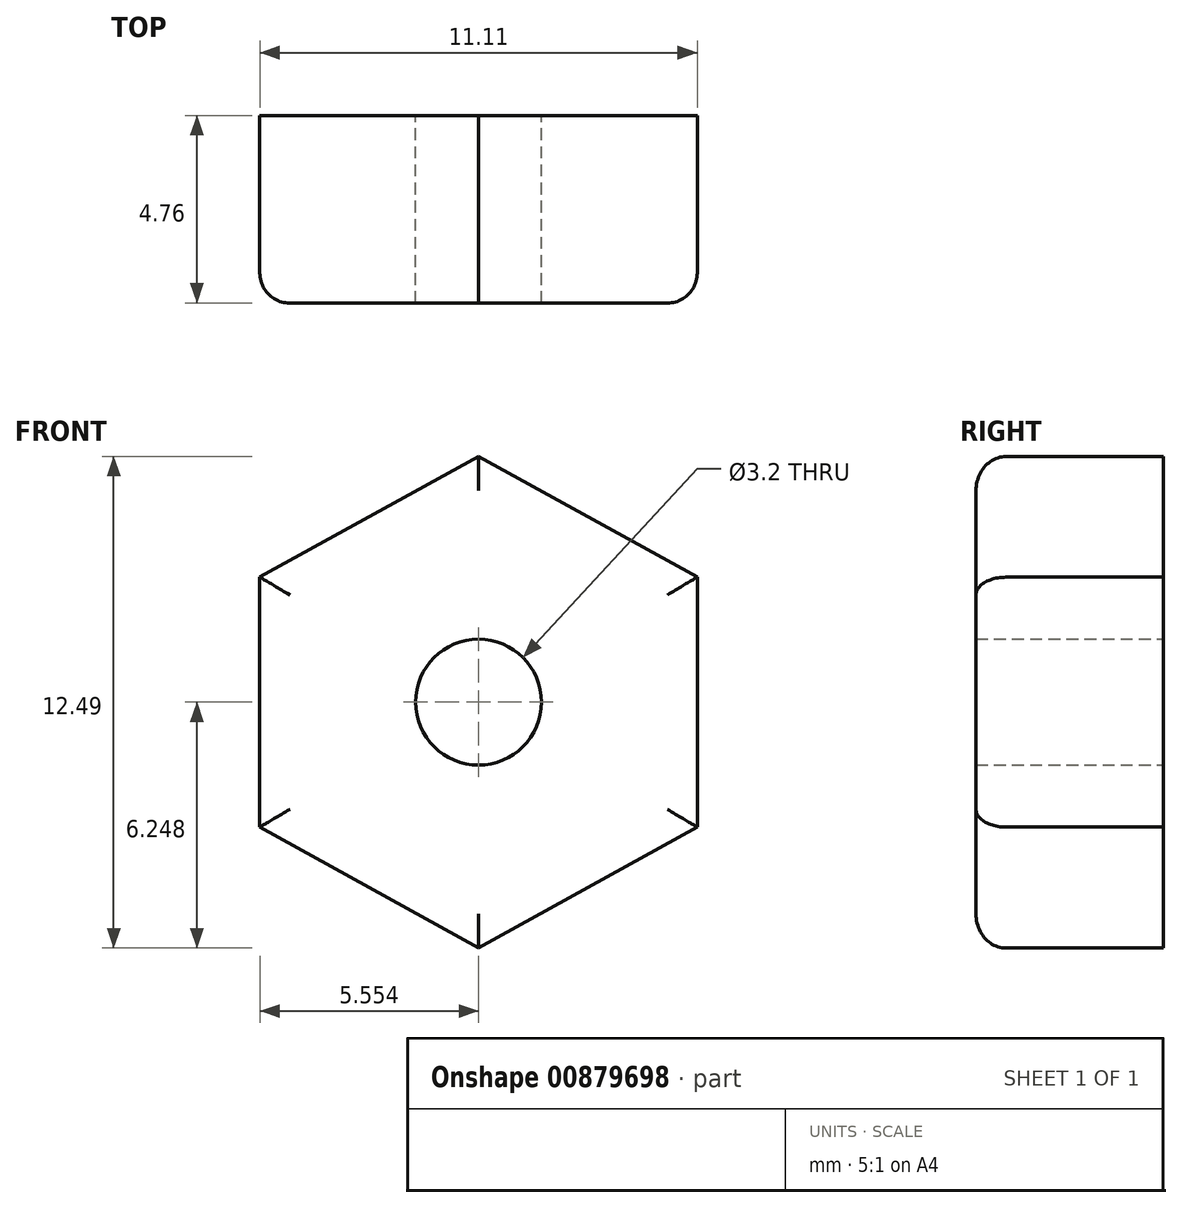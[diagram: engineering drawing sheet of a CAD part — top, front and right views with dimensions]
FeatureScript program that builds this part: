
annotation { "Feature Type Name" : "Feature", "Feature Type Description" : "" }
export const myFeature = defineFeature(function(context is Context, id is Id, definition is map)
    precondition{}
    {
        {
            var Q0;
            Q0=qCreatedBy(makeId("Front.planeOp"),FACE);
            var sketch = newSketch(context, id + "F0", { "sketchPlane" : qUnion([Q0])});
            skLineSegment(sketch, "E0.bottom", {"start": v(-47.1, 38.94) * mm, "end": v(-40.62, 38.94) * mm});
            skLineSegment(sketch, "E0.top", {"start": v(-47.1, 32.47) * mm, "end": v(-40.62, 32.47) * mm});
            skLineSegment(sketch, "E0.left", {"start": v(-47.1, 38.94) * mm, "end": v(-47.1, 32.47) * mm});
            skLineSegment(sketch, "E0.right", {"start": v(-40.62, 38.94) * mm, "end": v(-40.62, 32.47) * mm});
            skLineSegment(sketch, "E1", {"start": v(-43.86, 32.47) * mm, "end": v(-43.86, 38.94) * mm});
            skLineSegment(sketch, "E2", {"start": v(-47.1, 35.7) * mm, "end": v(-40.62, 35.7) * mm});
            skLineSegment(sketch, "E3", {"start": v(-43.86, 35.7) * mm, "end": v(-43.86, 29.7) * mm});
            skLineSegment(sketch, "E4", {"start": v(-43.86, 35.7) * mm, "end": v(-43.86, 41.7) * mm});
            skLineSegment(sketch, "E5", {"start": v(-43.86, 41.7) * mm, "end": v(-49.55, 38.88) * mm});
            skLineSegment(sketch, "E6", {"start": v(-49.55, 38.88) * mm, "end": v(-49.55, 32.53) * mm});
            skLineSegment(sketch, "E7", {"start": v(-49.55, 32.53) * mm, "end": v(-43.86, 29.7) * mm});
            skLineSegment(sketch, "E8", {"start": v(-43.86, 29.7) * mm, "end": v(-38.17, 32.53) * mm});
            skLineSegment(sketch, "E9", {"start": v(-38.17, 32.53) * mm, "end": v(-38.17, 38.88) * mm});
            skLineSegment(sketch, "E10", {"start": v(-38.17, 38.88) * mm, "end": v(-43.86, 41.7) * mm});
            skSolve(sketch);
        }
        {
            var Q0;
            Q0 = qSketchRegion(id + "F0", true);
            extrude(context, id + "F1", {"entities" : qUnion([Q0]), "depth" : 9.52 * mm, "offsetDistance" : 25.4 * mm});
        }
        {
            var Q0;
            Q0=makeQuery(id+"F1.opExtrude","SWEPT_BODY",BODY,{"disambiguationData":[OSD([sQuery(id+"F0.wireOp",EDGE,"E0.bottom"),sQuery(id+"F0.wireOp",EDGE,"E0.top"),sQuery(id+"F0.wireOp",EDGE,"E0.left"),sQuery(id+"F0.wireOp",EDGE,"E0.right"),sQuery(id+"F0.wireOp",EDGE,"E5"),sQuery(id+"F0.wireOp",EDGE,"E6"),sQuery(id+"F0.wireOp",EDGE,"E7"),sQuery(id+"F0.wireOp",EDGE,"E8"),sQuery(id+"F0.wireOp",EDGE,"E9"),sQuery(id+"F0.wireOp",EDGE,"E10")])]});
            deleteBodies(context, id + "F2", {"entities" : qUnion([Q0])});
        }
        {
            var Q0;
            Q0=qCreatedBy(makeId("Front.planeOp"),FACE);
            var sketch = newSketch(context, id + "F3", { "sketchPlane" : qUnion([Q0])});
            skLineSegment(sketch, "E11", {"start": v(-57.06, 29.06) * mm, "end": v(-57.06, 22.71) * mm});
            skLineSegment(sketch, "E12", {"start": v(-45.95, 29.06) * mm, "end": v(-45.95, 22.71) * mm});
            skLineSegment(sketch, "E13", {"start": v(-57.06, 29.06) * mm, "end": v(-51.5, 32.13) * mm});
            skLineSegment(sketch, "E14", {"start": v(-51.5, 32.13) * mm, "end": v(-45.95, 29.06) * mm});
            skLineSegment(sketch, "E15", {"start": v(-57.06, 22.71) * mm, "end": v(-51.5, 19.64) * mm});
            skLineSegment(sketch, "E16", {"start": v(-51.5, 19.64) * mm, "end": v(-45.95, 22.71) * mm});
            skCircle(sketch, "E17", {"center": v(-51.5, 25.89) * mm, "radius": 1.6 * mm});
            skSolve(sketch);
        }
        {
            var Q0;
            Q0 = qSketchRegion(id + "F3", true);
            extrude(context, id + "F4", {"entities" : qUnion([Q0]), "depth" : 4.76 * mm, "offsetDistance" : 25.4 * mm});
        }
        {
            var Q0;
            Q0=makeQuery(id+"F4.opExtrude","CAP_EDGE",EDGE,{"disambiguationData":[OSD([sQuery(id+"F3.wireOp",EDGE,"E13")])],"isStart":false});
            var Q1;
            Q1=makeQuery(id+"F4.opExtrude","CAP_EDGE",EDGE,{"disambiguationData":[OSD([sQuery(id+"F3.wireOp",EDGE,"E11")])],"isStart":false});
            var Q2;
            Q2=makeQuery(id+"F4.opExtrude","CAP_EDGE",EDGE,{"disambiguationData":[OSD([sQuery(id+"F3.wireOp",EDGE,"E15")])],"isStart":false});
            var Q3;
            Q3=makeQuery(id+"F4.opExtrude","CAP_EDGE",EDGE,{"disambiguationData":[OSD([sQuery(id+"F3.wireOp",EDGE,"E16")])],"isStart":false});
            var Q4;
            Q4=makeQuery(id+"F4.opExtrude","CAP_EDGE",EDGE,{"disambiguationData":[OSD([sQuery(id+"F3.wireOp",EDGE,"E12")])],"isStart":false});
            var Q5;
            Q5=makeQuery(id+"F4.opExtrude","CAP_EDGE",EDGE,{"disambiguationData":[OSD([sQuery(id+"F3.wireOp",EDGE,"E14")])],"isStart":false});
            fillet(context, id + "F5", {"entities" : qUnion([Q0, Q1, Q2, Q3, Q4, Q5]), "radius" : 0.76 * mm, "tangentPropagation" : true, "allowEdgeOverflow" : false});
        }
    });
